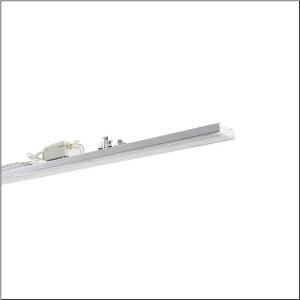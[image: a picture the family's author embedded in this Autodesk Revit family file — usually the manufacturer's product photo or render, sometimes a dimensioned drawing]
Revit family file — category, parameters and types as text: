
# Revit family: licross_21_recessed_ho_52tl11dv4l2s
name_source: partatom
category: Lighting Fixtures
units: mm (PartAtom-declared; Revit-internal decimal feet)

## family parameters
Cut with Voids When Loaded = No
Host = Face
Light Source = No
Part Type = Normal
Room Calculation Point = No
Round Connector Dimension = Use Diameter
Shared = No

## types (1)
- --- (1 x LED, 22660 lm, 125.6 W, 4000K)
    Apparent Load = 126 VA
    CIE Flux Codes = 87 95 99 100 100
    Color Rendering = 80
    Color Temperature = 4000K
    Default Elevation = 1800 mm
    Description = Licross 21 Recessed HO, luminaire insert, of sheet steel, galvanised, coil coated, white, length: 2.250mm, width: 66mm, height: 67mm, LED rated luminous flux: 22.660lm, light colour: 840, SDCM (Standard Deviation of Colour Matching)MacAdam ≤ 3 SDCM (initial), control gear: DALI 2, with plug, 5-pole, with phase selection, mains connection: 220..240V, AC, 50/60Hz, rated input power: 126W, internal wiring halogen-free, primary light control with lens, of plastic, primary optical cover: cover, of PMMA, light emission: direct distribution, primary light characteristic: symmetric, protection rating (complete): IP40, insulation class (complete): insulation class I (protective earthing), certification: CE, ENEC, VDE, UKCA, protection symbol: D if used in an environment without relevant dust loads with corresponding accessories, impact resistance: IK06, permissible ambient temperature for indoor applications: -40..+30°C, corresponds to IFS (International Featured Standards) requirements for safety and quality in the food industry, reducing of maximum allowable ambient temperature of 5°C with ceiling mounting, LABS conformity tested according to VDMA 24364:2018-05, The light source and the operating device comply with the requirements of the Ecodesign Regulation (EU) 2019/2020 and are replaceable in accordance with this regulation, packaging unit: 1 piece
    Height = 58 mm
    Lamp = 1 x LED
    Lamp Light Flux = 22660 lm
    Lamp Power = 125.6 W
    Lamp count = 1
    Length = 2250 mm
    Luminous efficacy = 180 lm/W
    Manufacturer = Siteco
    ModVariant = No
    Model = 52TL11DV4L2S
    Mounting Place = Ceiling
    Mounting Type = Pendant
    Number of Poles = 1
    OnlyDefault = Yes
    Power Factor = 1
    Product Name = Licross 21 Recessed HO
    Product group = luminaire insert | ceiling pendant
    ProductGroupID = 901
    Protection Class = Protection class I
    Protection Degree = IP 40
    RLX_Detail_Level = 1
    RLX_Emergency_Light_Flux = 0 lm
    RLX_Emergency_Type = 0
    RLX_Emergency_Type_DB = No
    RlxData = <blob elided: 29625 chars, md5=2578291c>
    Socket = socket
    Standby Power = 0 W
    System Light Flux = 22659 lm
    System Power = 126 W
    Type Comments = factory setting: luminous flux: 100 % | dim-lin: 254 | 489 mA
    Type Image = l_1296930.jpg
    URL = http://relux.com
    VarID = @adj_129143
    Voltage = 0 V
    Weight = 0.00 kg
    Width = 66 mm

## geometry (parser evidence)
native form markers: Blend x4, Sweep x11
no freeform markers — native parametric forms only
